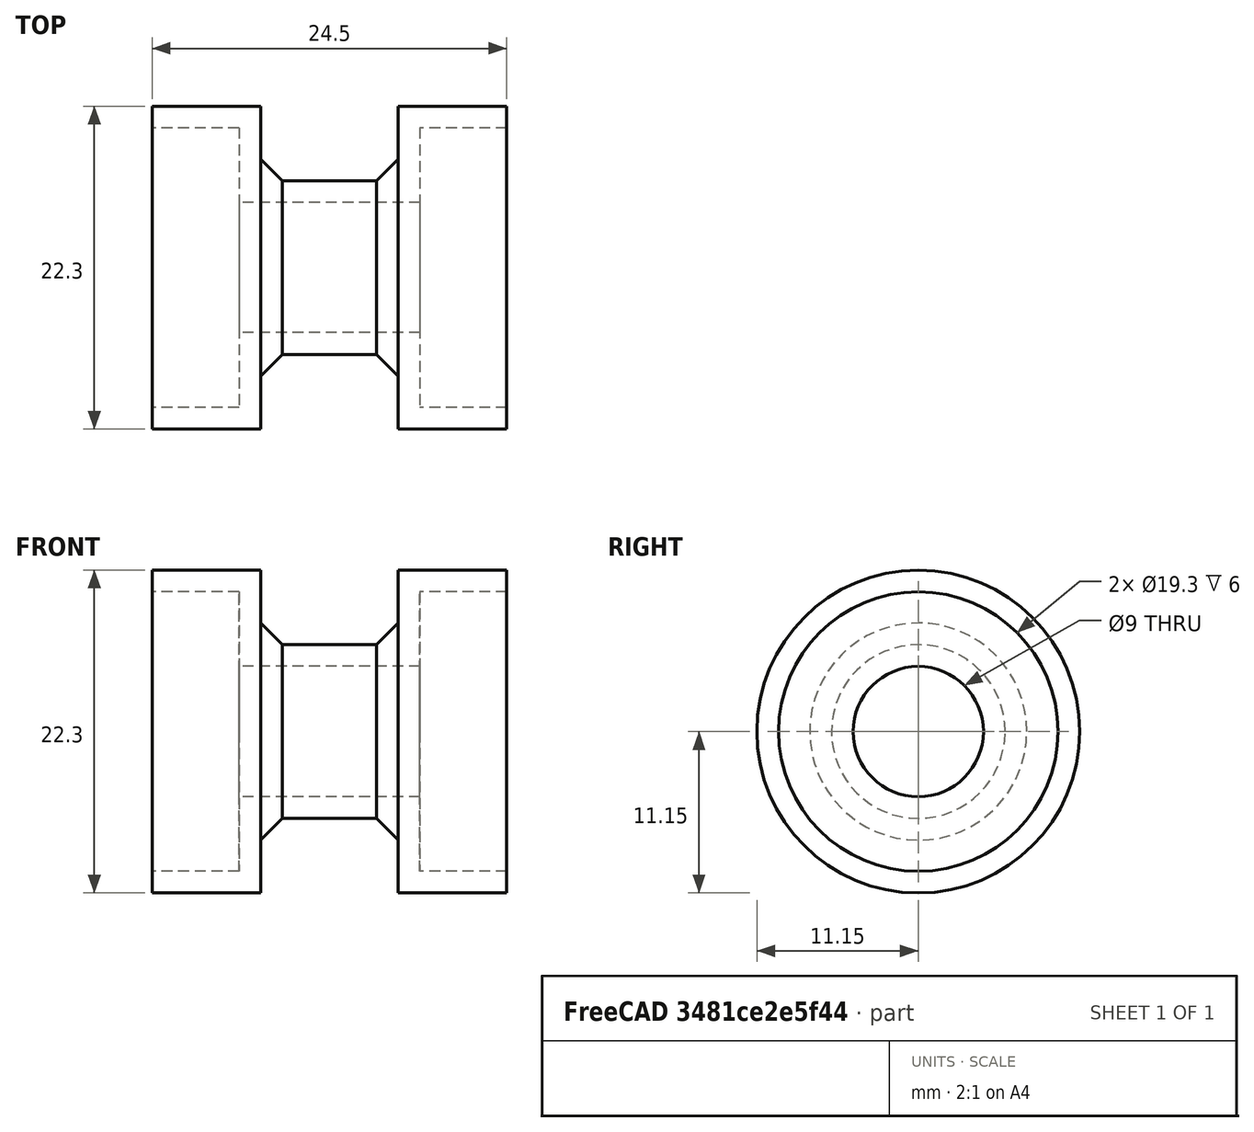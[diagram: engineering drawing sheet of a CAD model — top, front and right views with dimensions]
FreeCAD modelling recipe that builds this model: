
FCSTD DOCUMENT  (FreeCAD 0.19R)
Label: y-belt-tensioner-v3
License: All rights reserved
LicenseURL: http://en.wikipedia.org/wiki/All_rights_reserved
objects: Sketcher::SketchObject×1, PartDesign::Revolution×1, PartDesign::Body×1
note: 4 computed .brp shape members not serialized (recipe doc carries the construction recipe); baked Part::Feature solids carry a one-line shape summary decoded from their .brp

FEATURE [Sketcher::SketchObject] Sketch
  MapMode = 5
  Support = -> [XY_Plane]
  sketch-geometry (14):
    g0: LineSegment StartX=0 StartY=11.15 StartZ=0 EndX=7.5 EndY=11.15 EndZ=0
    g1: LineSegment StartX=9 StartY=6 StartZ=0 EndX=15.5 EndY=6 EndZ=0
    g2: LineSegment StartX=17 StartY=11.15 StartZ=0 EndX=24.5 EndY=11.15 EndZ=0
    g3: LineSegment StartX=24.5 StartY=11.15 StartZ=0 EndX=24.5 EndY=9.65 EndZ=0
    g4: LineSegment StartX=24.5 StartY=9.65 StartZ=0 EndX=18.5 EndY=9.65 EndZ=0
    g5: LineSegment StartX=18.5 StartY=9.65 StartZ=0 EndX=18.5 EndY=4.5 EndZ=0
    g6: LineSegment StartX=18.5 StartY=4.5 StartZ=0 EndX=6 EndY=4.5 EndZ=0
    g7: LineSegment StartX=6 StartY=4.5 StartZ=0 EndX=6 EndY=9.65 EndZ=0
    g8: LineSegment StartX=6 StartY=9.65 StartZ=0 EndX=0 EndY=9.65 EndZ=0
    g9: LineSegment StartX=0 StartY=9.65 StartZ=0 EndX=0 EndY=11.15 EndZ=0
    g10: LineSegment StartX=15.5 StartY=6 StartZ=0 EndX=17 EndY=7.5 EndZ=0
    g11: LineSegment StartX=17 StartY=7.5 StartZ=0 EndX=17 EndY=11.15 EndZ=0
    g12: LineSegment StartX=7.5 StartY=11.15 StartZ=0 EndX=7.5 EndY=7.5 EndZ=0
    g13: LineSegment StartX=7.5 StartY=7.5 StartZ=0 EndX=9 EndY=6 EndZ=0
  constraints (42):
    c: Horizontal(g0)
    c: Horizontal(g1)
    c: Horizontal(g2)
    c: Coincident(g2,g3)
    c: Coincident(g3,g4)
    c: Coincident(g4,g5)
    c: Vertical(g5)
    c: Coincident(g5,g6)
    c: Horizontal(g6)
    c: Coincident(g6,g7)
    c: Coincident(g7,g8)
    c: Coincident(g8,g9)
    c: Coincident(g9,g0)
    c: Horizontal(g8)
    c: Horizontal(g4)
    c: Vertical(g7)
    c: Vertical(g3)
    c: Vertical(g9)
    c: Equal(g2,g0)
    c: Equal(g9,g3)
    c: Equal(g7,g5)
    c: Equal(g8,g4)
    c: DistanceY(g9,g9) = 1.5
    c: DistanceX(g8,g8) = 6
    c: DistanceX(g1,g1) = 6.5
    c: DistanceX(g2,g4) = 1.5
    c: DistanceY(g-1,g8) = 9.65
    c: PointOnObject(g8,g-2)
    c: DistanceY(g-1,g1) = 6
    c: Coincident(g1,g10)
    c: Coincident(g10,g11)
    c: Coincident(g11,g2)
    c: Vertical(g11)
    c: Coincident(g0,g12)
    c: Vertical(g12)
    c: Coincident(g12,g13)
    c: Coincident(g13,g1)
    c: Equal(g13,g10)
    c: Equal(g12,g11)
    c: DistanceX(g1,g10) = 1.5
    c: DistanceY(g1,g10) = 1.5
    c: DistanceY(g6,g1) = 1.5
FEATURE [PartDesign::Revolution] Revolution
  Angle = 360
  Axis = (1,0,0)
  Base = (0,0,0)
  Profile = -> Sketch
  ReferenceAxis = -> X_Axis
  Reversed = true
FEATURE [PartDesign::Body] Body
  Group = -> [Sketch,Revolution]
  Origin = -> Origin
  Tip = -> Revolution
